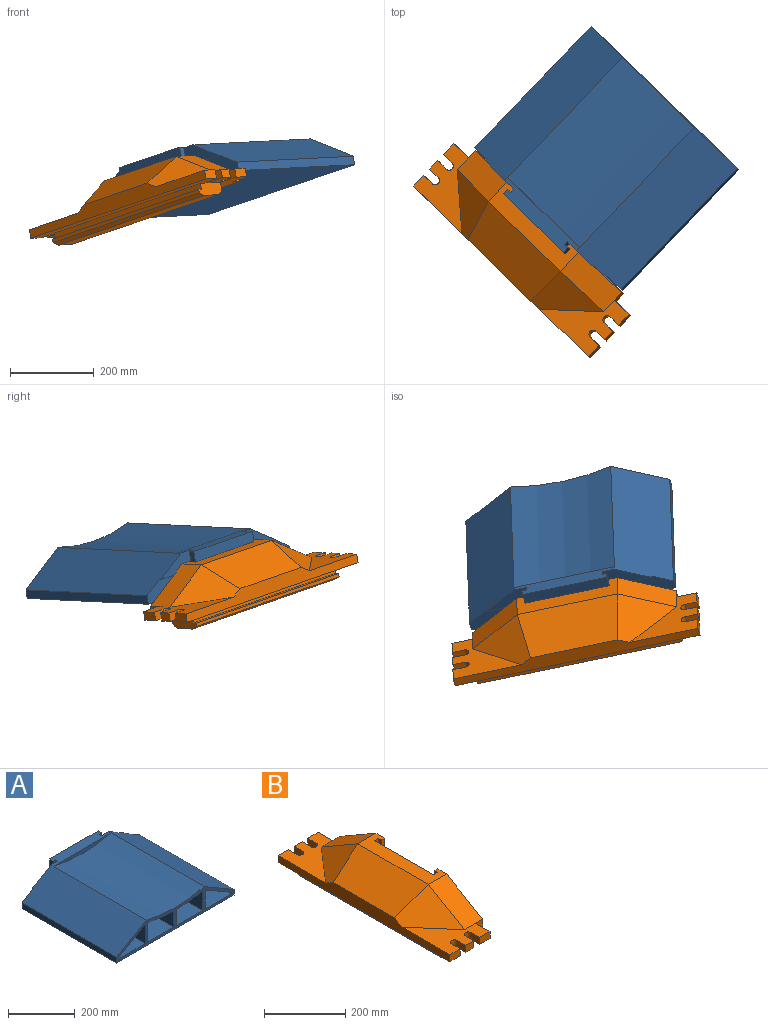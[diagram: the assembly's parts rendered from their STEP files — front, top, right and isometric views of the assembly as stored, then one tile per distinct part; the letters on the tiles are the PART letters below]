
ASSEMBLY  parts=2 mates=1
PART A: 46 faces, bbox 500x430x94.2 mm
  f0: plane 206x15mm, normal (0,0,-1), area 1230mm2, adj f20,f21,f22,f23,f24,f25,f26,f33
  f1: plane 381x113mm, normal (0,0,1), area 43053mm2, adj f2,f17,f37,f45
  f2: plane 113x70.34mm, normal (0,-1,0), area 4262.7mm2, adj f1,f3,f37,f45
  f3: plane 381x113mm, normal (-0.5,0,-0.87), area 49713.3mm2, adj f2,f17,f37,f45
  f4: plane 381x112mm, normal (0,0,1), area 42672mm2, adj f6,f17,f41,f42
  f5: cylinder r=521.8mm len=381mm, axis (0,-1,0), area 43054.2mm2, adj f6,f17,f41,f42
  f6: plane 112x72.49mm, normal (0,-1,0), area 7145.9mm2, adj f4,f5,f41,f42
  f7: plane 381x112mm, normal (0,0,1), area 42672mm2, adj f9,f17,f40,f44
  f8: cylinder r=521.8mm len=381mm, axis (0,-1,0), area 43054.2mm2, adj f9,f17,f40,f44
  f9: plane 112x72.49mm, normal (0,-1,0), area 7145.9mm2, adj f7,f8,f40,f44
  f10: plane 186x5mm, normal (0,0,-1), area 930mm2, adj f20,f24,f30,f32
  f11: plane 400x20.88mm, normal (1,0,0), area 8350.6mm2, adj f14,f17,f19,f29
  f12: plane 108.83x45.52mm, normal (0,1,0), area 3159.5mm2, adj f15,f16,f20,f31
  f13: plane 400x20.88mm, normal (-1,0,0), area 8350.6mm2, adj f15,f17,f19,f29
  f14: plane 405x127mm, normal (0.5,0,0.87), area 59113.9mm2, adj f11,f16,f17,f18,f27,f29,f31
  f15: plane 405x127mm, normal (-0.5,0,0.87), area 59113.9mm2, adj f12,f13,f16,f17,f27,f29,f31
  f16: plane 246x35mm, normal (0,0,1), area 7410mm2, adj f12,f14,f15,f18,f20,f21,f22,f23
  f17: plane 500x94.2mm, normal (0,-1,0), area 12503.4mm2, adj f1,f3,f4,f5,f7,f8,f11,f13
  f18: plane 108.83x45.52mm, normal (0,1,0), area 3159.5mm2, adj f14,f16,f24,f31
  f19: plane 500x400mm, normal (0,0,-1), area 200000mm2, adj f11,f13,f17,f29
  f20: plane 56.71x20mm, normal (-1,0,0), area 617.1mm2, adj f0,f10,f12,f16,f23,f30,f32,f33
  f21: plane 206x46.71mm, normal (0,1,0), area 9623.1mm2, adj f0,f16,f22,f26
  f22: plane 46.71x15mm, normal (-1,0,0), area 700.7mm2, adj f0,f16,f21,f23
  f23: plane 46.71x10mm, normal (0,-1,0), area 467.1mm2, adj f0,f16,f20,f22
  f24: plane 56.71x20mm, normal (1,0,0), area 617.1mm2, adj f0,f10,f16,f18,f25,f30,f32,f33
  f25: plane 46.71x10mm, normal (0,-1,0), area 467.1mm2, adj f0,f16,f24,f26
  f26: plane 46.71x15mm, normal (1,0,0), area 700.7mm2, adj f0,f16,f21,f25
  f27: cylinder r=511.8mm len=395mm, axis (0,-1,0), area 98130.6mm2, adj f14,f15,f17,f28
  f28: plane 246x15mm, normal (0,-1,0), area 2467.3mm2, adj f16,f27
  f29: plane 500x48.69mm, normal (0,1,0), area 23003.1mm2, adj f11,f13,f14,f15,f19,f31
  f30: plane 186x1.2mm, normal (0,-1,0), area 223mm2, adj f10,f20,f24,f31
  f31: plane 403.67x5mm, normal (0,0,-1), area 2018.3mm2, adj f12,f14,f15,f18,f29,f30
  f32: plane 186x10mm, normal (0,-1,0), area 1860mm2, adj f10,f20,f24,f34
  f33: plane 186x10mm, normal (0,1,0), area 1860mm2, adj f0,f20,f24,f34
  f34: plane 186x15mm, normal (0,0,-1), area 2790mm2, adj f20,f24,f32,f33
  f35: plane 381x5.1mm, normal (1,0,0), area 1944.2mm2, adj f17,f36,f38,f39
  f36: plane 381x113mm, normal (0,0,1), area 43053mm2, adj f17,f35,f39,f43
  f37: plane 381x5.1mm, normal (-1,0,0), area 1944.2mm2, adj f1,f2,f3,f17
  f38: plane 381x113mm, normal (0.5,0,-0.87), area 49713.3mm2, adj f17,f35,f39,f43
  f39: plane 113x70.34mm, normal (0,-1,0), area 4262.7mm2, adj f35,f36,f38,f43
  f40: plane 381x59.22mm, normal (1,0,0), area 22564.3mm2, adj f7,f8,f9,f17
  f41: plane 381x59.22mm, normal (-1,0,0), area 22564.3mm2, adj f4,f5,f6,f17
  f42: plane 381x72.49mm, normal (1,0,0), area 27617.3mm2, adj f4,f5,f6,f17
  f43: plane 381x70.34mm, normal (-1,0,0), area 26800.9mm2, adj f17,f36,f38,f39
  f44: plane 381x72.49mm, normal (-1,0,0), area 27617.3mm2, adj f7,f8,f9,f17
  f45: plane 381x70.34mm, normal (1,0,0), area 26800.9mm2, adj f1,f2,f3,f17
PART B: 50 faces, bbox 165x600x124.2 mm
  f0: plane 28x20.88mm, normal (0,1,0), area 584.5mm2, adj f4,f5,f45,f48
  f1: plane 36x20.88mm, normal (0,1,0), area 751.6mm2, adj f4,f5,f14,f44
  f2: plane 36x20.88mm, normal (0,-1,0), area 751.6mm2, adj f4,f6,f14,f42
  f3: plane 28x20.88mm, normal (0,-1,0), area 584.5mm2, adj f4,f6,f38,f41
  f4: plane 600x165mm, normal (0,0,-1), area 53521.7mm2, adj f0,f1,f2,f3,f8,f9,f10,f11
  f5: plane 167x140mm, normal (0,0,1), area 11413.4mm2, adj f0,f1,f14,f21,f24,f25,f35,f44
  f6: plane 167x140mm, normal (0,0,1), area 11413.4mm2, adj f2,f3,f14,f20,f26,f27,f37,f38
  f7: plane 246x63.68mm, normal (0,0,1), area 10714.1mm2, adj f8,f13,f20,f21,f28,f29,f30,f31
  f8: plane 157x94.2mm, normal (1,0,0), area 10133.4mm2, adj f4,f7,f12,f21,f28
  f9: plane 80x30mm, normal (0,-1,0), area 2111.7mm2, adj f4,f15,f16,f17,f18,f19,f22,f23
  f10: plane 25x20.88mm, normal (0,-1,0), area 521.9mm2, adj f4,f13,f20,f26
  f11: plane 80x30mm, normal (0,1,0), area 2111.7mm2, adj f4,f15,f16,f17,f18,f19,f22,f23
  f12: plane 25x20.88mm, normal (0,1,0), area 521.9mm2, adj f4,f8,f21,f25
  f13: plane 157x94.2mm, normal (1,0,0), area 10133.4mm2, adj f4,f7,f10,f20,f34
  f14: plane 600x35.7mm, normal (-1,0,0), area 16088.4mm2, adj f1,f2,f4,f5,f6,f35,f36,f37
  f15: plane 500x15mm, normal (-1,0,0), area 7500mm2, adj f4,f9,f11,f16
  f16: plane 500x10mm, normal (0,0,1), area 5000mm2, adj f9,f11,f15,f17
  f17: plane 500x8.01mm, normal (-1,0,0), area 4002.7mm2, adj f9,f11,f16,f23
  f18: plane 500x45mm, normal (0,0,-1), area 22500mm2, adj f9,f11,f22,f23
  f19: plane 500x10mm, normal (1,0,0), area 5000mm2, adj f4,f9,f11,f22
  f20: plane 127x73.32mm, normal (0,-0.5,0.87), area 9337.7mm2, adj f6,f7,f10,f13,f37
  f21: plane 127x73.32mm, normal (0,0.5,0.87), area 9337.7mm2, adj f5,f7,f8,f12,f35
  f22: cylinder r=20mm len=500mm, axis (0,1,0), area 15708mm2, adj f9,f11,f18,f19
  f23: plane 500x15mm, normal (-0.42,0,-0.91), area 8275.3mm2, adj f9,f11,f17,f18
  f24: plane 36x20.88mm, normal (0,1,0), area 751.6mm2, adj f4,f5,f25,f47
  f25: plane 50x20.88mm, normal (1,0,0), area 1043.8mm2, adj f4,f5,f12,f24
  f26: plane 50x20.88mm, normal (1,0,0), area 1043.8mm2, adj f4,f6,f10,f27
  f27: plane 36x20.88mm, normal (0,-1,0), area 751.6mm2, adj f4,f6,f26,f39
  f28: plane 94.2x10mm, normal (0,-1,0), area 942mm2, adj f4,f7,f8,f29
  f29: plane 94.2x10mm, normal (-1,0,0), area 942mm2, adj f4,f7,f28,f30
  f30: plane 94.2x15mm, normal (0,-1,0), area 1413mm2, adj f4,f7,f29,f31
  f31: plane 206x94.2mm, normal (1,0,0), area 19405.2mm2, adj f4,f7,f30,f32
  f32: plane 94.2x15mm, normal (0,1,0), area 1413mm2, adj f4,f7,f31,f33
  f33: plane 94.2x10mm, normal (-1,0,0), area 942mm2, adj f4,f7,f32,f34
  f34: plane 94.2x10mm, normal (0,1,0), area 942mm2, adj f4,f7,f13,f33
  f35: plane 142.68x101.33mm, normal (-0.5,0.43,0.75), area 10313.2mm2, adj f5,f14,f21,f36
  f36: plane 246x101.33mm, normal (-0.5,0,0.87), area 26948mm2, adj f7,f14,f35,f37
  f37: plane 142.68x101.33mm, normal (-0.5,-0.43,0.75), area 10313.2mm2, adj f6,f14,f20,f36
  f38: plane 30x20.88mm, normal (1,0,0), area 626.3mm2, adj f3,f4,f6,f40
  f39: plane 30x20.88mm, normal (-1,0,0), area 626.3mm2, adj f4,f6,f27,f40
  f40: cylinder r=10mm len=20.88mm, axis (0,0,1), area 655.9mm2, adj f4,f6,f38,f39
  f41: plane 30x20.88mm, normal (-1,0,0), area 626.3mm2, adj f3,f4,f6,f43
  f42: plane 30x20.88mm, normal (1,0,0), area 626.3mm2, adj f2,f4,f6,f43
  f43: cylinder r=10mm len=20.88mm, axis (0,0,1), area 655.9mm2, adj f4,f6,f41,f42
  f44: plane 30x20.88mm, normal (1,0,0), area 626.3mm2, adj f1,f4,f5,f46
  f45: plane 30x20.88mm, normal (-1,0,0), area 626.3mm2, adj f0,f4,f5,f46
  f46: cylinder r=10mm len=20.88mm, axis (0,0,1), area 655.9mm2, adj f4,f5,f44,f45
  f47: plane 30x20.88mm, normal (-1,0,0), area 626.3mm2, adj f4,f5,f24,f49
  f48: plane 30x20.88mm, normal (1,0,0), area 626.3mm2, adj f0,f4,f5,f49
  f49: cylinder r=10mm len=20.88mm, axis (0,0,1), area 655.9mm2, adj f4,f5,f47,f48
PLACE A rot(axis=(-0.13,0.03,0.99),136.3deg) t=(-95.57,-158.9,293.19)mm
PLACE B rot(axis=(-0.25,-0.15,0.95),47.9deg) t=(-376.85,-102.95,166.27)mm
MATE slider A.f16 <-> B.f7  axis (-0.19,0.14,0.97) through (-203.31,-364.54,398.14)mm
